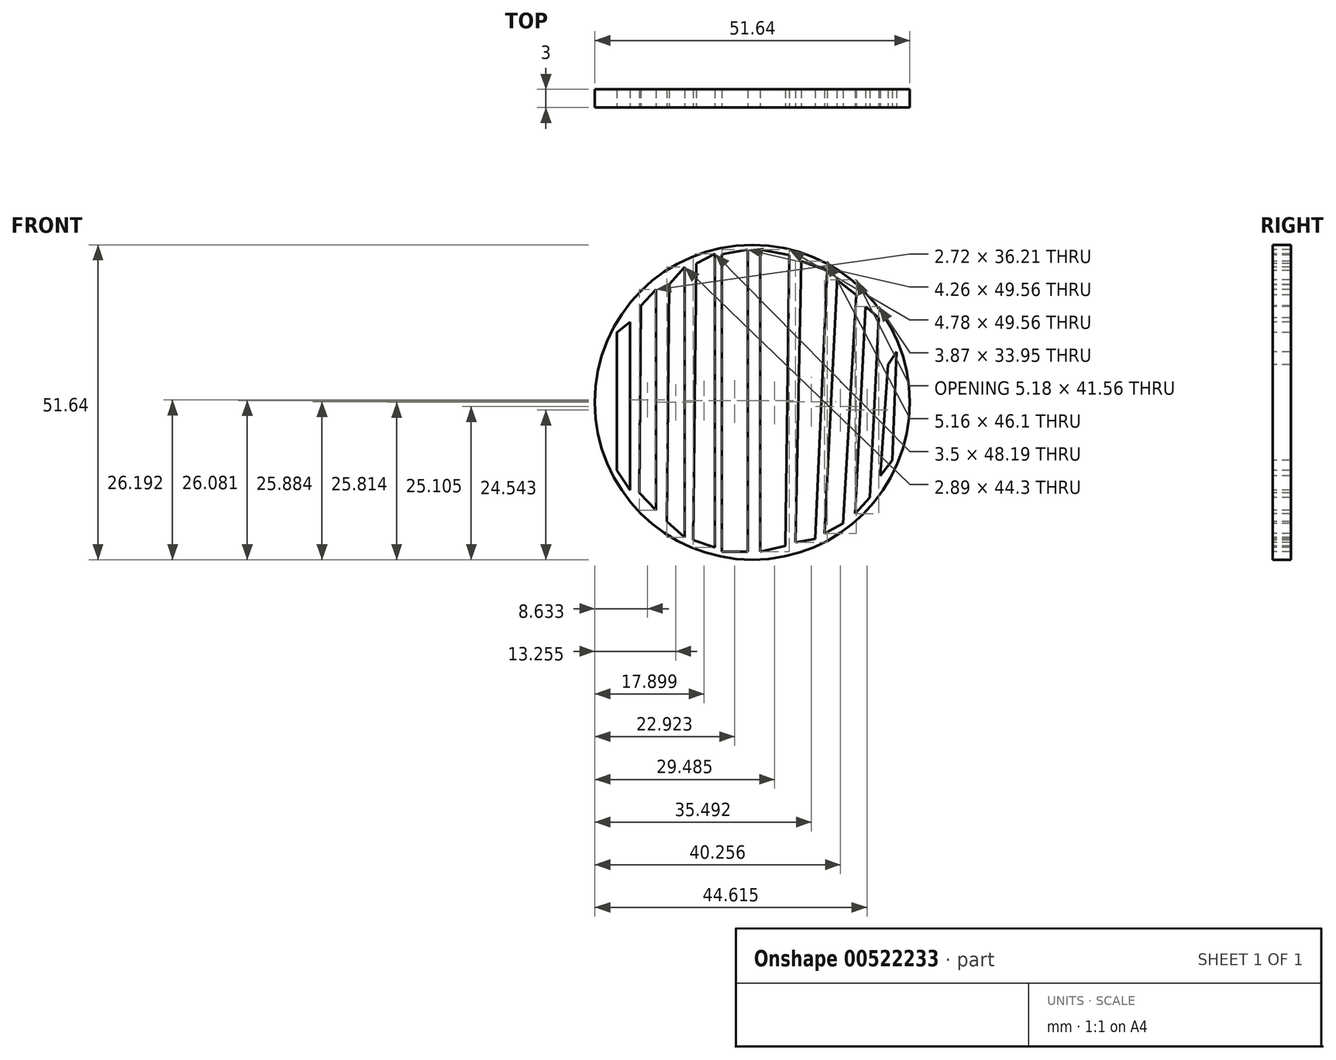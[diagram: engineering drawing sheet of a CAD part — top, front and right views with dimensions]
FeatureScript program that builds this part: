
annotation { "Feature Type Name" : "Feature", "Feature Type Description" : "" }
export const myFeature = defineFeature(function(context is Context, id is Id, definition is map)
    precondition{}
    {
        {
            var Q0;
            Q0=qCreatedBy(makeId("Front.planeOp"),FACE);
            var sketch = newSketch(context, id + "F0", { "sketchPlane" : qUnion([Q0])});
            skCircle(sketch, "E0", {"center": v(0, 0) * mm, "radius": 25.82 * mm});
            skSolve(sketch);
        }
        {
            var Q0;
            Q0=makeQuery(id+"F0.imprint","IMPRINT",FACE,{"disambiguationData":[TD([[makeQuery(id+"F0.imprint","IMPRINT",EDGE,{"derivedFrom":sQuery(id+"F0.wireOp",EDGE,"E0")}),1.0]])]});
            extrude(context, id + "F1", {"entities" : qUnion([Q0]), "depth" : 3 * mm, "offsetDistance" : 25 * mm});
        }
        {
            var Q0;
            Q0=makeQuery(id+"F1.opExtrude","CAP_FACE",FACE,{"disambiguationData":[OSD([sQuery(id+"F0.wireOp",EDGE,"E0")])],"isStart":false});
            var sketch = newSketch(context, id + "F2", { "sketchPlane" : qUnion([Q0])});
            skLineSegment(sketch, "E1", {"start": v(-22.23, -11.2) * mm, "end": v(-22.23, 11.41) * mm});
            skLineSegment(sketch, "E2", {"start": v(-22.23, 11.41) * mm, "end": v(-20.02, 13.16) * mm});
            skLineSegment(sketch, "E3", {"start": v(-20.02, 13.16) * mm, "end": v(-20.02, -14.4) * mm});
            skLineSegment(sketch, "E4", {"start": v(-20.02, -14.4) * mm, "end": v(-22.23, -11.2) * mm});
            skLineSegment(sketch, "E5", {"start": v(-17.74, 17.5) * mm, "end": v(-17.74, -16.9) * mm});
            skLineSegment(sketch, "E6", {"start": v(-17.74, -16.9) * mm, "end": v(-15.53, -19.42) * mm});
            skLineSegment(sketch, "E7", {"start": v(-15.53, -19.42) * mm, "end": v(-15.53, 19.1) * mm});
            skLineSegment(sketch, "E8", {"start": v(-15.53, 19.1) * mm, "end": v(-17.66, 17.43) * mm});
            skLineSegment(sketch, "E9", {"start": v(-13.63, 19.33) * mm, "end": v(-11.12, 22.15) * mm});
            skLineSegment(sketch, "E10", {"start": v(-11.12, 22.15) * mm, "end": v(-11.12, -22.16) * mm});
            skLineSegment(sketch, "E11", {"start": v(-11.12, -22.16) * mm, "end": v(-14.01, -19.57) * mm});
            skLineSegment(sketch, "E12", {"start": v(-14.01, -19.57) * mm, "end": v(-13.63, 19.33) * mm});
            skLineSegment(sketch, "E13", {"start": v(-9.22, 22.76) * mm, "end": v(-6.17, 24.35) * mm});
            skLineSegment(sketch, "E14", {"start": v(-6.17, 24.35) * mm, "end": v(-6.17, -23.83) * mm});
            skLineSegment(sketch, "E15", {"start": v(-6.17, -23.83) * mm, "end": v(-9.67, -22.61) * mm});
            skLineSegment(sketch, "E16", {"start": v(-9.67, -22.61) * mm, "end": v(-9.22, 22.76) * mm});
            skLineSegment(sketch, "E17", {"start": v(-0.77, 25.04) * mm, "end": v(-5.03, 24.28) * mm});
            skLineSegment(sketch, "E18", {"start": v(-5.03, 24.28) * mm, "end": v(-5.03, -24.52) * mm});
            skLineSegment(sketch, "E19", {"start": v(-5.03, -24.52) * mm, "end": v(-0.77, -24.52) * mm});
            skLineSegment(sketch, "E20", {"start": v(-0.77, -24.52) * mm, "end": v(-0.77, 25.04) * mm});
            skLineSegment(sketch, "E21", {"start": v(6.05, 24.13) * mm, "end": v(1.28, 25.04) * mm});
            skLineSegment(sketch, "E22", {"start": v(1.28, 25.04) * mm, "end": v(1.28, -24.52) * mm});
            skLineSegment(sketch, "E23", {"start": v(1.28, -24.52) * mm, "end": v(5.44, -23.53) * mm});
            skLineSegment(sketch, "E24", {"start": v(5.44, -23.53) * mm, "end": v(6.05, 24.13) * mm});
            skLineSegment(sketch, "E25", {"start": v(7.98, 23.11) * mm, "end": v(12.25, 21.59) * mm});
            skLineSegment(sketch, "E26", {"start": v(12.25, 21.59) * mm, "end": v(10.32, -22.4) * mm});
            skLineSegment(sketch, "E27", {"start": v(10.32, -22.4) * mm, "end": v(7.1, -22.99) * mm});
            skLineSegment(sketch, "E28", {"start": v(7.1, -22.99) * mm, "end": v(7.98, 23.11) * mm});
            skLineSegment(sketch, "E29", {"start": v(13.88, 20.06) * mm, "end": v(17.03, 17.63) * mm});
            skLineSegment(sketch, "E30", {"start": v(17.03, 17.63) * mm, "end": v(14.9, -19.87) * mm});
            skLineSegment(sketch, "E31", {"start": v(14.9, -19.87) * mm, "end": v(11.84, -21.5) * mm});
            skLineSegment(sketch, "E32", {"start": v(11.84, -21.5) * mm, "end": v(13.88, 19.25) * mm});
            skLineSegment(sketch, "E33", {"start": v(13.88, 19.25) * mm, "end": v(13.88, 20.06) * mm});
            skLineSegment(sketch, "E34", {"start": v(18.55, 15.7) * mm, "end": v(16.86, -18.25) * mm});
            skLineSegment(sketch, "E35", {"start": v(16.86, -18.25) * mm, "end": v(19.26, -15.6) * mm});
            skLineSegment(sketch, "E36", {"start": v(19.26, -15.6) * mm, "end": v(20.73, 13.85) * mm});
            skLineSegment(sketch, "E37", {"start": v(20.73, 13.85) * mm, "end": v(18.55, 15.7) * mm});
            skLineSegment(sketch, "E38", {"start": v(22.2, 6.14) * mm, "end": v(20.99, -12.04) * mm});
            skLineSegment(sketch, "E39", {"start": v(20.99, -12.04) * mm, "end": v(22.92, -9.5) * mm});
            skLineSegment(sketch, "E40", {"start": v(22.92, -9.5) * mm, "end": v(23.63, 8.28) * mm});
            skLineSegment(sketch, "E41", {"start": v(23.63, 8.28) * mm, "end": v(22.2, 6.14) * mm});
            skSolve(sketch);
        }
        {
            var Q0;
            Q0 = qSketchRegion(id + "F2", true);
            extrude(context, id + "F3", {"entities" : qUnion([Q0]), "operationType" : NewBodyOperationType.REMOVE, "oppositeDirection" : true, "depth" : 25 * mm, "offsetDistance" : 25 * mm});
        }
        {
            var Q0;
            Q0=makeQuery(id+"F1.opExtrude","CAP_FACE",FACE,{"disambiguationData":[OSD([sQuery(id+"F0.wireOp",EDGE,"E0")])],"isStart":false});
            var sketch = newSketch(context, id + "F4", { "sketchPlane" : qUnion([Q0])});
            skLineSegment(sketch, "E42", {"start": v(-18.25, 15.82) * mm, "end": v(-18.55, -14.83) * mm});
            skLineSegment(sketch, "E43", {"start": v(-18.55, -14.83) * mm, "end": v(-15.83, -17.73) * mm});
            skLineSegment(sketch, "E44", {"start": v(-15.83, -17.73) * mm, "end": v(-15.83, 18.48) * mm});
            skLineSegment(sketch, "E45", {"start": v(-15.83, 18.48) * mm, "end": v(-18.25, 15.82) * mm});
            skSolve(sketch);
        }
        {
            var Q0;
            Q0=makeQuery(id+"F4.imprint","IMPRINT",FACE,{"disambiguationData":[TD([[makeQuery(id+"F4.imprint","IMPRINT",EDGE,{"derivedFrom":sQuery(id+"F4.wireOp",EDGE,"E42")}),1.0]])]});
            extrude(context, id + "F5", {"entities" : qUnion([Q0]), "operationType" : NewBodyOperationType.REMOVE, "oppositeDirection" : true, "depth" : 25 * mm, "offsetDistance" : 25 * mm});
        }
    });
